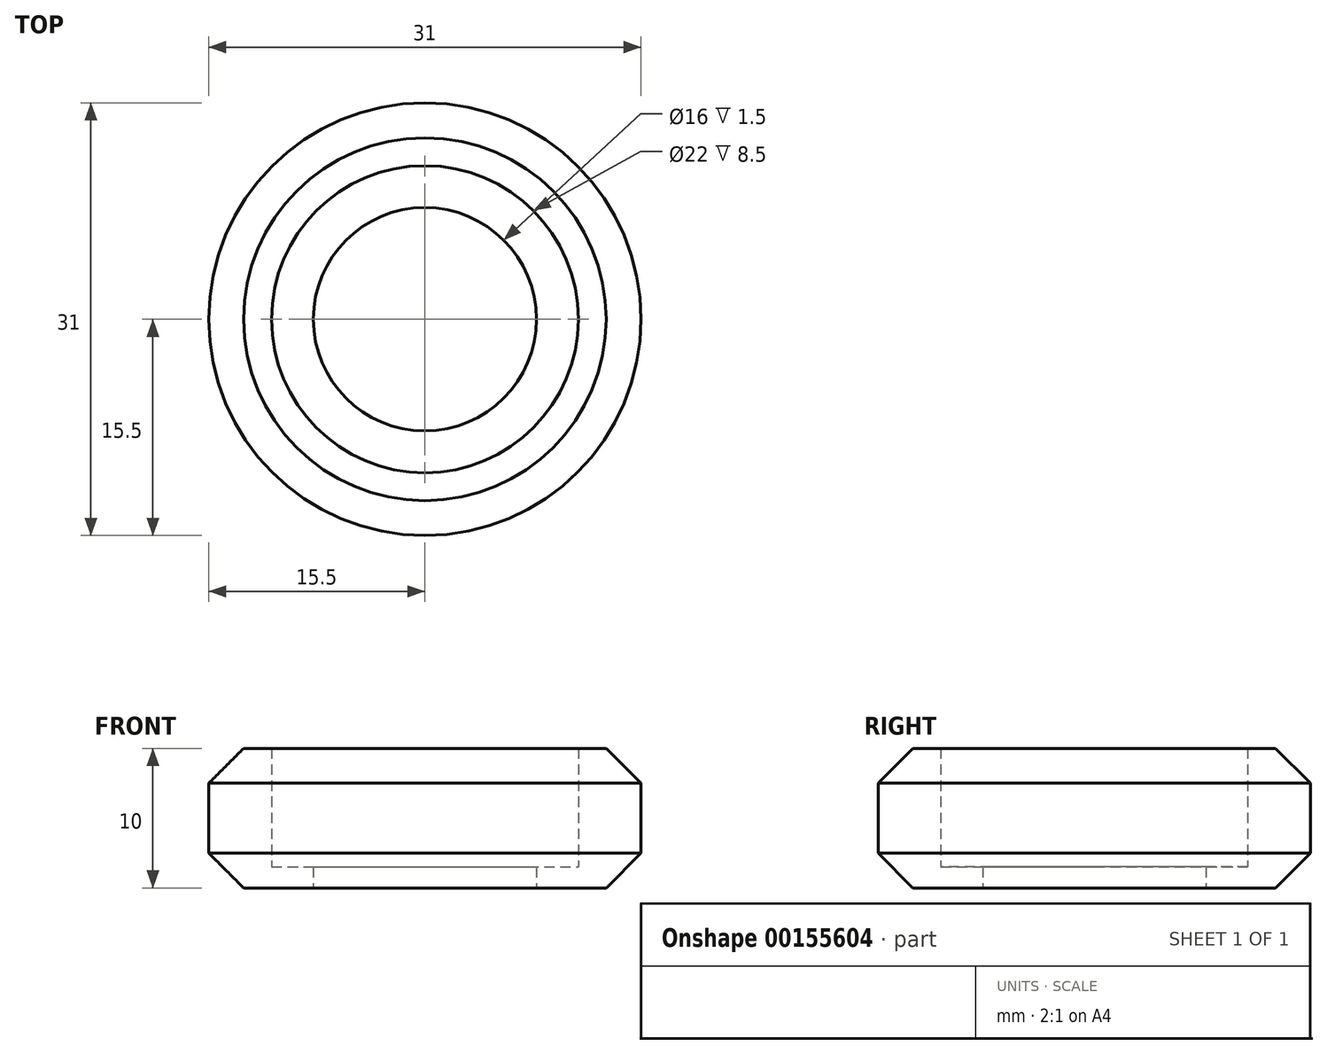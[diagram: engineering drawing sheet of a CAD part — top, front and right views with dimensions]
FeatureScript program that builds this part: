
annotation { "Feature Type Name" : "Feature", "Feature Type Description" : "" }
export const myFeature = defineFeature(function(context is Context, id is Id, definition is map)
    precondition{}
    {
        {
            var Q0;
            Q0=qCreatedBy(makeId("Front.planeOp"),FACE);
            var sketch = newSketch(context, id + "F0", { "sketchPlane" : qUnion([Q0])});
            skLineSegment(sketch, "E0.bottom", {"start": v(0, 0) * mm, "end": v(2, 0) * mm});
            skLineSegment(sketch, "E0.top", {"start": v(0, 10) * mm, "end": v(2, 10) * mm});
            skLineSegment(sketch, "E0.left", {"start": v(0, 0) * mm, "end": v(0, 10) * mm});
            skLineSegment(sketch, "E0.right", {"start": v(2, 0) * mm, "end": v(2, 10) * mm});
            skLineSegment(sketch, "E1", {"start": v(0, 0) * mm, "end": v(-5, 5) * mm});
            skLineSegment(sketch, "E2", {"start": v(-5, 5) * mm, "end": v(0, 10) * mm});
            skLineSegment(sketch, "E3.bottom", {"start": v(2, 0) * mm, "end": v(13, 0) * mm, "construction": true});
            skLineSegment(sketch, "E3.top", {"start": v(2, 10) * mm, "end": v(13, 10) * mm, "construction": true});
            skLineSegment(sketch, "E3.left", {"start": v(2, 0) * mm, "end": v(2, 10) * mm, "construction": true});
            skLineSegment(sketch, "E3.right", {"start": v(13, 0) * mm, "end": v(13, 10) * mm, "construction": true});
            skLineSegment(sketch, "E4", {"start": v(-2.5, 2.5) * mm, "end": v(-2.5, 7.5) * mm});
            skLineSegment(sketch, "E5.bottom", {"start": v(2, 0) * mm, "end": v(5, 0) * mm});
            skLineSegment(sketch, "E5.top", {"start": v(2, 1.5) * mm, "end": v(5, 1.5) * mm});
            skLineSegment(sketch, "E5.left", {"start": v(2, 0) * mm, "end": v(2, 1.5) * mm});
            skLineSegment(sketch, "E5.right", {"start": v(5, 0) * mm, "end": v(5, 1.5) * mm});
            skSolve(sketch);
        }
        {
            var Q0;
            {var subQ0=sQuery(id+"F0.wireOp",EDGE,"E0.left");Q0=makeQuery(id+"F0.imprint","IMPRINT",FACE,{"disambiguationData":[TD([[makeQuery(id+"F0.imprint","IMPRINT",EDGE,{"derivedFrom":subQ0}),1.0]])]});}
            var Q1;
            Q1=makeQuery(id+"F0.imprint","IMPRINT",FACE,{"disambiguationData":[TD([[makeQuery(id+"F0.imprint","IMPRINT",EDGE,{"derivedFrom":sQuery(id+"F0.wireOp",EDGE,"E0.bottom")}),1.0]])]});
            var Q2;
            Q2=makeQuery(id+"F0.imprint","IMPRINT",FACE,{"disambiguationData":[TD([[makeQuery(id+"F0.imprint","IMPRINT",EDGE,{"derivedFrom":sQuery(id+"F0.wireOp",EDGE,"E5.bottom")}),1.0]])]});
            var Q3;
            Q3=sQuery(id+"F0.wireOp",EDGE,"E3.right");
            revolve(context, id + "F1", {"entities" : qUnion([Q0, Q1, Q2]), "axis" : qUnion([Q3]), "revolveType" : RevolveType.FULL});
        }
    });
